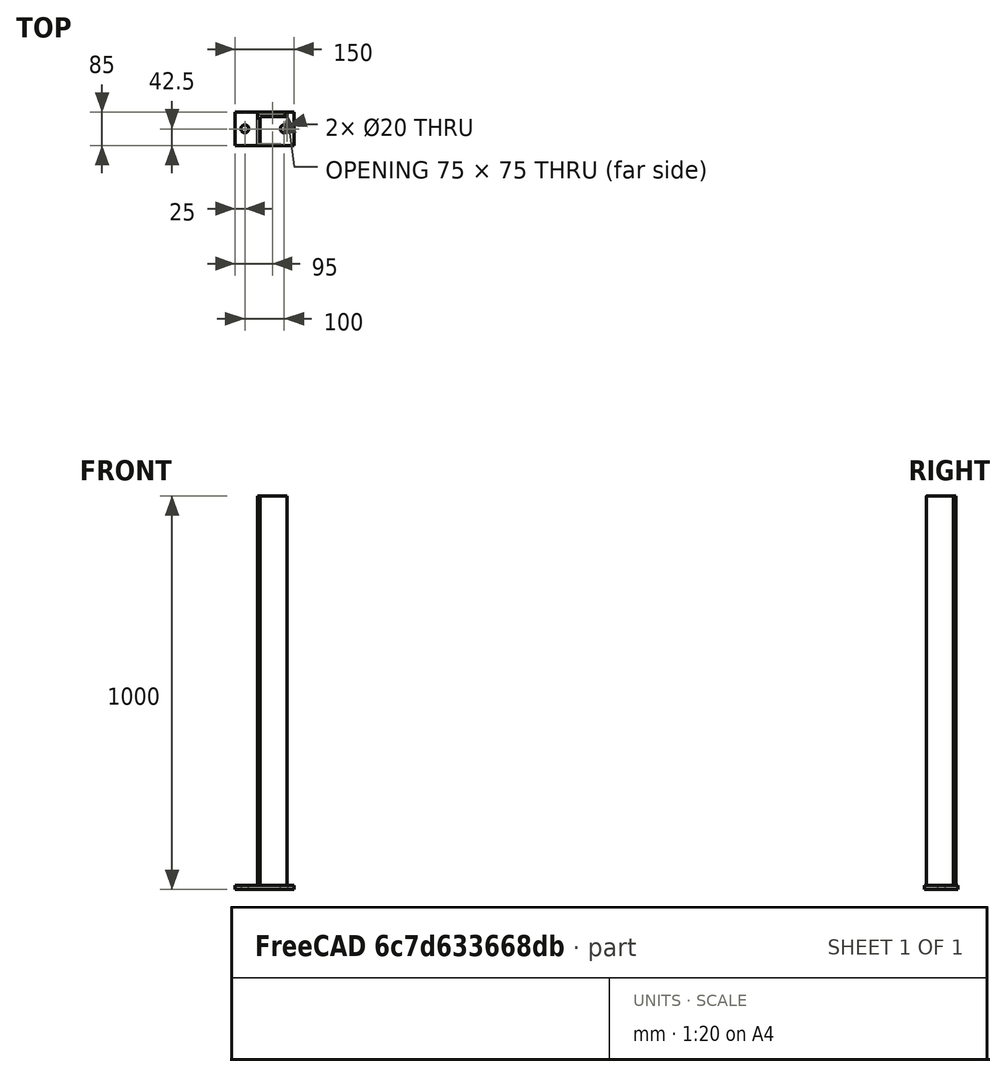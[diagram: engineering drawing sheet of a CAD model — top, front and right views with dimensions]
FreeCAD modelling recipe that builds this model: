
FCSTD DOCUMENT  (FreeCAD 0.21R30492 (Git))
Label: 03_Pst_L
License: All rights reserved
LicenseURL: http://en.wikipedia.org/wiki/All_rights_reserved
objects: Part::FeaturePython×2, Part::Extrusion×1, Part::MultiFuse×1
note: 4 computed .brp shape members not serialized (recipe doc carries the construction recipe); baked Part::Feature solids carry a one-line shape summary decoded from their .brp

FEATURE [Part::FeaturePython] BasePlate  # WARN: FeaturePython — macro-defined, semantics opaque (R4)
  B = 150
  D = 20
  H = 85
  Placement = pos=(-20,0,0) rot=(0,0,1;0rad)
  b1 = 25
  h1 = 42.5
  sface = 0
FEATURE [Part::Extrusion] Extrude  label="BasePlate001"
  Base = -> BasePlate
  Dir = (0,0,1)
  DirMode = 2
  FaceMakerClass = Part::FaceMakerBullseye
  LengthFwd = 10
  LengthRev = 0
  Solid = true
  Symmetric = false
FEATURE [Part::FeaturePython] Angle  # WARN: FeaturePython — macro-defined, semantics opaque (R4)
  A = 75
  B = 75
  L = 1000
  Solid = true
  g0 = 7.85
  mass = 6.85021
  size = 10
  standard = SS_Equal
FEATURE [Part::MultiFuse] Fusion
  Shapes = -> [Extrude,Angle]
